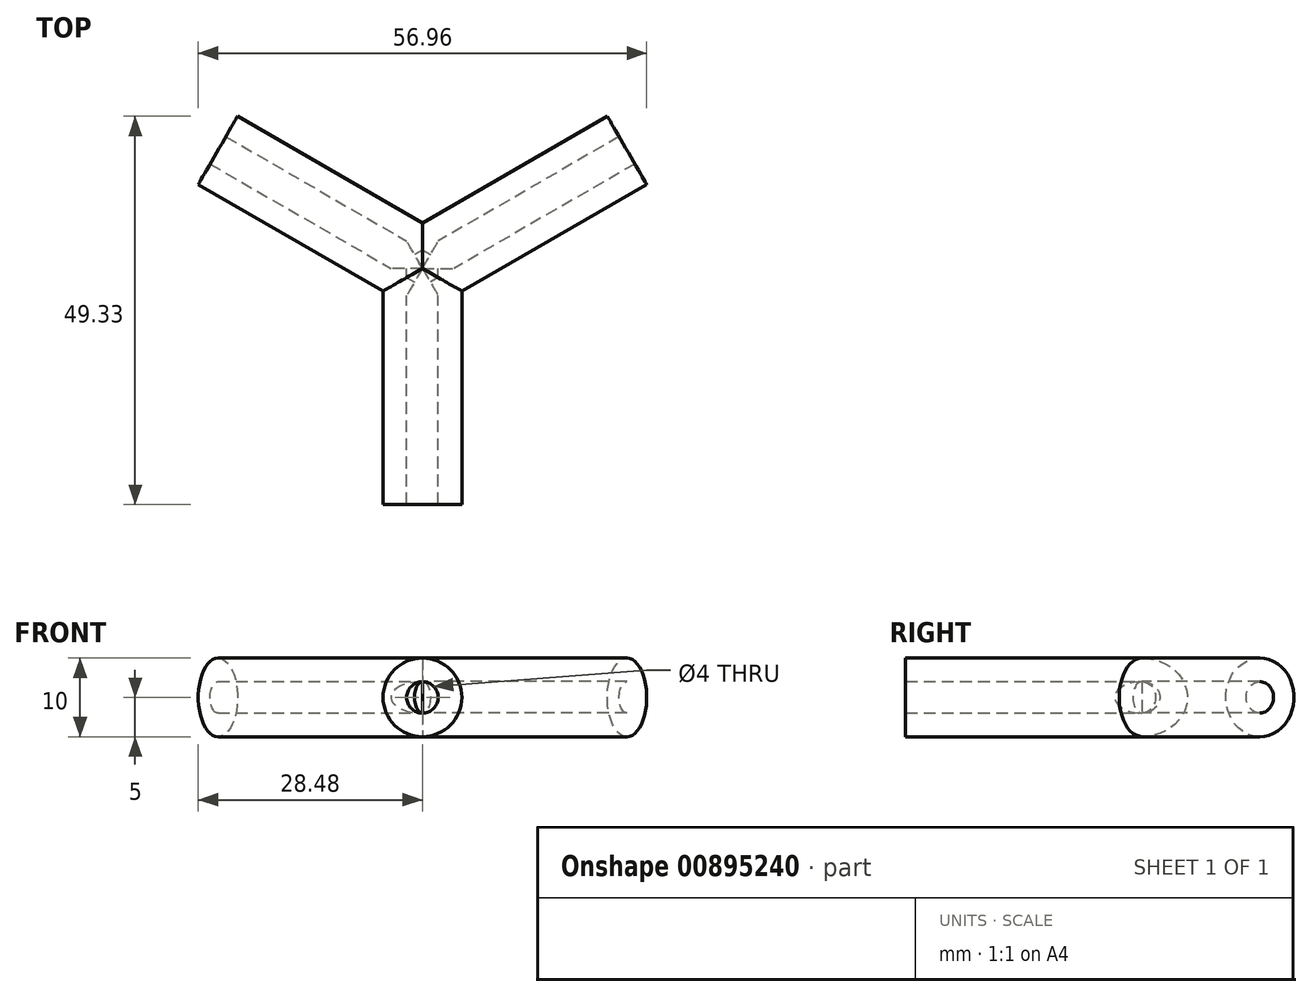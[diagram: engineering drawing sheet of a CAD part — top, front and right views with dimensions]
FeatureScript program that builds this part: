
annotation { "Feature Type Name" : "Feature", "Feature Type Description" : "" }
export const myFeature = defineFeature(function(context is Context, id is Id, definition is map)
    precondition{}
    {
        {
            var Q0;
            Q0=qCreatedBy(makeId("Front.planeOp"),FACE);
            var sketch = newSketch(context, id + "F0", { "sketchPlane" : qUnion([Q0])});
            skCircle(sketch, "E0", {"center": v(0, 0) * mm, "radius": 5 * mm});
            skCircle(sketch, "E1", {"center": v(0, 0) * mm, "radius": 2 * mm});
            skSolve(sketch);
        }
        {
            var Q0;
            Q0 = qSketchRegion(id + "F0", true);
            extrude(context, id + "F1", {"entities" : qUnion([Q0]), "depth" : 30 * mm, "offsetDistance" : 25 * mm});
        }
        {
            var Q0;
            Q0=qCreatedBy(makeId("Front.planeOp"),FACE);
            var sketch = newSketch(context, id + "F2", { "sketchPlane" : qUnion([Q0])});
            skLineSegment(sketch, "E2", {"start": v(0, 0) * mm, "end": v(0, 70.28) * mm});
            skSolve(sketch);
        }
        {
            var Q0;
            Q0=makeQuery(id+"F1.opExtrude","SWEPT_BODY",BODY,{"disambiguationData":[OSD([sQuery(id+"F0.wireOp",EDGE,"E0")])]});
            var Q1;
            Q1=sQuery(id+"F2.wireOp",EDGE,"E2");
            circularPattern(context, id + "F3", {"operationType" : NewBodyOperationType.ADD, "entities" : qUnion([Q0]), "axis" : qUnion([Q1]), "angle" : 360 * degree, "instanceCount" : 3, "equalSpace" : true});
        }
    });
